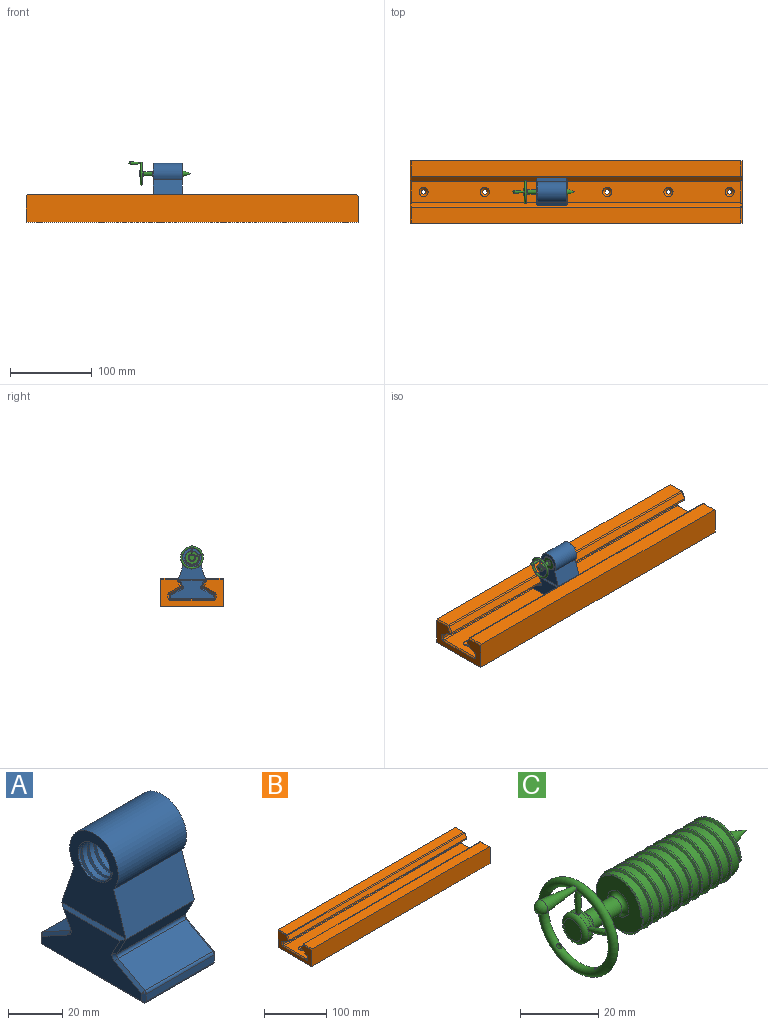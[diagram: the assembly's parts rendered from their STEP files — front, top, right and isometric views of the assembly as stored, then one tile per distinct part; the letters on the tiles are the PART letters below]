
ASSEMBLY  parts=3 mates=5
PART A: 54 faces, bbox 39.1x55.6x64.5 mm
  f0: plane 39.75x34.11mm, normal (1,0,0), area 733.2mm2, adj f44,f45,f46,f47,f48,f50,f51
  f1: plane 35.56x9.01mm, normal (0,0.88,-0.47), area 362.6mm2, adj f10,f26,f36,f44
  f2: plane 35.56x14.05mm, normal (0,0.48,0.88), area 569.9mm2, adj f10,f11,f22,f32
  f3: plane 35.56x3.32mm, normal (0,1,0), area 118mm2, adj f11,f12,f18,f31
  f4: plane 52.07x35.56mm, normal (0,0,-1), area 1851.6mm2, adj f12,f13,f17,f35
  f5: plane 35.56x3.32mm, normal (0,-1,0), area 118mm2, adj f13,f14,f21,f39
  f6: plane 35.56x14.05mm, normal (0,-0.48,0.88), area 569.9mm2, adj f14,f15,f25,f43
  f7: plane 35.56x9.01mm, normal (0,-0.88,-0.47), area 362.6mm2, adj f15,f29,f40,f46
  f8: plane 52.07x21.59mm, normal (1,0,0), area 724.5mm2, adj f31,f32,f34,f35,f36,f38,f39,f40
  f9: plane 52.07x21.59mm, normal (-1,0,0), area 724.5mm2, adj f17,f18,f21,f22,f24,f25,f26,f27
  f10: cylinder r=1.27mm len=35.56mm, axis (1,0,0), area 70.3mm2, adj f1,f2,f24,f34
  f11: cylinder r=1.27mm len=35.56mm, axis (-1,0,0), area 48.3mm2, adj f2,f3,f20,f30
  f12: cylinder r=1.27mm len=35.56mm, axis (1,0,0), area 70.9mm2, adj f3,f4,f16,f33
  f13: cylinder r=1.27mm len=35.56mm, axis (-1,0,0), area 70.9mm2, adj f4,f5,f19,f37
  f14: cylinder r=1.27mm len=35.56mm, axis (-1,0,0), area 48.3mm2, adj f5,f6,f23,f41
  f15: cylinder r=1.27mm len=35.56mm, axis (1,0,0), area 70.3mm2, adj f6,f7,f27,f42
  f16: cone r=1.27mm half-angle=45deg, axis (1,0,0), area 1.2mm2, adj f12,f17,f18
  f17: plane 52.07x1.27mm, normal (-0.71,0,-0.71), area 93.5mm2, adj f4,f9,f16,f19
  f18: plane 4.29x2.24mm, normal (-0.71,0.71,0), area 6mm2, adj f3,f9,f16,f20
  f19: cone r=1.27mm half-angle=45deg, axis (1,0,0), area 1.8mm2, adj f13,f17,f21
  f20: cone r=1.27mm half-angle=45deg, axis (1,0,0), area 1.8mm2, adj f11,f18,f22
  f21: plane 3.32x1.27mm, normal (-0.71,-0.71,0), area 6mm2, adj f5,f9,f19,f23
  f22: plane 14.66x8.83mm, normal (-0.71,0.34,0.62), area 28.8mm2, adj f2,f9,f20,f24
  f23: cone r=1.27mm half-angle=45deg, axis (1,0,0), area 1.2mm2, adj f14,f21,f25
  f24: cone r=2.54mm half-angle=45deg, axis (-1,0,0), area 5.3mm2, adj f9,f10,f22,f26
  f25: plane 14.66x8.83mm, normal (-0.71,-0.34,0.62), area 28.8mm2, adj f6,f9,f23,f27
  f26: plane 9.01x5.9mm, normal (-0.71,0.62,-0.33), area 16.4mm2, adj f1,f9,f24,f28
  f27: cone r=2.54mm half-angle=45deg, axis (-1,0,0), area 5.3mm2, adj f9,f15,f25,f29
  f28: plane 33.74x1.27mm, normal (-0.71,0,0.71), area 56.8mm2, adj f9,f26,f29,f49
  f29: plane 9.01x5.9mm, normal (-0.71,-0.62,-0.33), area 16.4mm2, adj f7,f9,f27,f28
  f30: cone r=1.27mm half-angle=45deg, axis (-1,0,0), area 0.8mm2, adj f11,f31,f32
  f31: plane 4.29x2.24mm, normal (0.71,0.71,0), area 6mm2, adj f3,f8,f30,f33
  f32: plane 14.98x9.14mm, normal (0.71,0.34,0.62), area 28.8mm2, adj f2,f8,f30,f34
  f33: cone r=1.27mm half-angle=45deg, axis (-1,0,0), area 2.4mm2, adj f12,f31,f35
  f34: cone r=2.54mm half-angle=45deg, axis (1,0,0), area 5.3mm2, adj f8,f10,f32,f36
  f35: plane 52.07x1.27mm, normal (0.71,0,-0.71), area 93.5mm2, adj f4,f8,f33,f37
  f36: plane 9.01x5.9mm, normal (0.71,0.62,-0.33), area 16.4mm2, adj f1,f8,f34,f38
  f37: cone r=1.27mm half-angle=45deg, axis (-1,0,0), area 1.8mm2, adj f13,f35,f39
  f38: plane 33.74x1.27mm, normal (0.71,0,0.71), area 56.8mm2, adj f8,f36,f40,f45
  f39: plane 3.32x1.27mm, normal (0.71,-0.71,0), area 6mm2, adj f5,f8,f37,f41
  f40: plane 9.01x5.9mm, normal (0.71,-0.62,-0.33), area 16.4mm2, adj f7,f8,f38,f42
  f41: cone r=1.27mm half-angle=45deg, axis (-1,0,0), area 1.2mm2, adj f14,f39,f43
  f42: cone r=2.54mm half-angle=45deg, axis (1,0,0), area 5.3mm2, adj f8,f15,f40,f43
  f43: plane 14.66x8.83mm, normal (0.71,-0.34,0.62), area 28.8mm2, adj f6,f8,f41,f42
  f44: plane 35.66x19.23mm, normal (0,0.95,0.32), area 724.6mm2, adj f0,f1,f45,f47,f49
  f45: plane 33.74x0.1mm, normal (0,0,-1), area 3.4mm2, adj f0,f38,f44,f46
  f46: plane 35.66x19.23mm, normal (0,-0.95,0.32), area 724.6mm2, adj f0,f7,f45,f47,f49
  f47: cylinder r=12.7mm len=35.66mm, axis (-1,0,0), area 1990.1mm2, adj f0,f44,f46,f49
  f48: cylinder r=8.26mm len=35.66mm, axis (-1,0,0), area 1233.4mm2, adj f0,f49,f50,f51,f52,f53
  f49: plane 39.87x34.23mm, normal (-1,0,0), area 732.3mm2, adj f28,f44,f46,f47,f48,f52,f53
  f50: plane 1.27x0.69mm, normal (0,0,1), area 0.4mm2, adj f0,f48,f53
  f51: bspline ~36.26x22mm, area 774.1mm2, adj f0,f48,f52,f53
  f52: plane 1.27x0.6mm, normal (0,0,-1), area 0.4mm2, adj f48,f49,f51
  f53: bspline ~36.35x22mm, area 798.9mm2, adj f48,f49,f50,f51
PART B: 68 faces, bbox 406.4x76.2x34.3 mm
  f0: plane 402.84x18.95mm, normal (0,0,1), area 7635.8mm2, adj f4,f21,f22,f67
  f1: plane 76.2x32.26mm, normal (1,0,0), area 1262.6mm2, adj f3,f4,f6,f51,f53,f55,f56,f57
  f2: plane 76.2x32.77mm, normal (-1,0,0), area 1345.9mm2, adj f3,f4,f6,f22,f23,f24,f25,f26
  f3: plane 406.4x34.29mm, normal (0,-1,0), area 13932.2mm2, adj f1,f2,f5,f6,f38,f51
  f4: plane 406.4x34.29mm, normal (0,1,0), area 13932.2mm2, adj f0,f1,f2,f6,f22,f67
  f5: plane 402.84x18.95mm, normal (0,0,1), area 7635.8mm2, adj f3,f14,f38,f51
  f6: plane 406.4x76.2mm, normal (0,0,-1), area 30809.2mm2, adj f1,f2,f3,f4,f39,f41,f43,f45
  f7: plane 402.84x7.64mm, normal (0,0.88,0.47), area 3486.2mm2, adj f14,f15,f36,f53
  f8: plane 402.84x12.78mm, normal (0,0.48,-0.88), area 5871.1mm2, adj f15,f16,f34,f55
  f9: plane 402.84x3.12mm, normal (0,1,0), area 1255.1mm2, adj f16,f17,f32,f57
  f10: plane 402.84x51.82mm, normal (0,0,1), area 20282.6mm2, adj f17,f18,f30,f40,f42,f44,f46,f48
  f11: plane 402.84x3.12mm, normal (0,-1,0), area 1255.1mm2, adj f18,f19,f28,f61
  f12: plane 402.84x12.78mm, normal (0,-0.48,-0.88), area 5871.1mm2, adj f19,f20,f26,f63
  f13: plane 402.84x7.64mm, normal (0,-0.88,0.47), area 3486.2mm2, adj f20,f21,f24,f65
  f14: cylinder r=2.03mm len=402.84mm, axis (-1,0,0), area 886.4mm2, adj f5,f7,f37,f52
  f15: cylinder r=2.03mm len=402.84mm, axis (1,0,0), area 1274.2mm2, adj f7,f8,f35,f54
  f16: cylinder r=2.03mm len=402.84mm, axis (-1,0,0), area 874.8mm2, adj f8,f9,f33,f56
  f17: cylinder r=2.03mm len=402.84mm, axis (-1,0,0), area 1285.8mm2, adj f9,f10,f31,f58
  f18: cylinder r=2.03mm len=402.84mm, axis (1,0,0), area 1285.8mm2, adj f10,f11,f29,f60
  f19: cylinder r=2.03mm len=402.84mm, axis (-1,0,0), area 874.8mm2, adj f11,f12,f27,f62
  f20: cylinder r=2.03mm len=402.84mm, axis (1,0,0), area 1274.2mm2, adj f12,f13,f25,f64
  f21: cylinder r=2.03mm len=402.84mm, axis (1,0,0), area 886.4mm2, adj f0,f13,f23,f66
  f22: plane 18.95x1.52mm, normal (-0.71,0,0.71), area 40.9mm2, adj f0,f2,f4,f23
  f23: cone r=0.51mm half-angle=45deg, axis (1,0,0), area 3mm2, adj f2,f21,f22,f24
  f24: plane 8.36x5.4mm, normal (-0.71,-0.62,0.33), area 18.7mm2, adj f2,f13,f23,f25
  f25: cone r=0.51mm half-angle=45deg, axis (1,0,0), area 4.3mm2, adj f2,f20,f24,f26
  f26: plane 13.51x8.35mm, normal (-0.71,-0.34,-0.62), area 31.4mm2, adj f2,f12,f25,f27
  f27: cone r=3.56mm half-angle=45deg, axis (-1,0,0), area 6.4mm2, adj f2,f19,f26,f28
  f28: plane 3.12x1.52mm, normal (-0.71,-0.71,0), area 6.7mm2, adj f2,f11,f27,f29
  f29: cone r=3.56mm half-angle=45deg, axis (-1,0,0), area 9.5mm2, adj f2,f18,f28,f30
  f30: plane 51.82x1.52mm, normal (-0.71,0,0.71), area 111.7mm2, adj f2,f10,f29,f31
  f31: cone r=3.56mm half-angle=45deg, axis (-1,0,0), area 9.5mm2, adj f2,f17,f30,f32
  f32: plane 3.12x1.52mm, normal (-0.71,0.71,0), area 6.7mm2, adj f2,f9,f31,f33
  f33: cone r=3.56mm half-angle=45deg, axis (-1,0,0), area 6.4mm2, adj f2,f16,f32,f34
  f34: plane 13.51x8.35mm, normal (-0.71,0.34,-0.62), area 31.4mm2, adj f2,f8,f33,f35
  f35: cone r=0.51mm half-angle=45deg, axis (1,0,0), area 4.3mm2, adj f2,f15,f34,f36
  f36: plane 8.36x5.4mm, normal (-0.71,0.62,0.33), area 18.7mm2, adj f2,f7,f35,f37
  f37: cone r=0.51mm half-angle=45deg, axis (1,0,0), area 3mm2, adj f2,f14,f36,f38
  f38: plane 18.95x1.52mm, normal (-0.71,0,0.71), area 40.9mm2, adj f2,f3,f5,f37
  f39: cylinder r=2.9mm len=6.19mm, axis (0,0,1), area 112.8mm2, adj f6,f40
  f40: cone r=2.9mm half-angle=45deg, axis (0,0,1), area 102mm2, adj f10,f39
  f41: cylinder r=2.9mm len=6.19mm, axis (0,0,1), area 112.8mm2, adj f6,f42
  f42: cone r=2.9mm half-angle=45deg, axis (0,0,1), area 102mm2, adj f10,f41
  f43: cylinder r=2.9mm len=6.19mm, axis (0,0,1), area 112.8mm2, adj f6,f44
  f44: cone r=2.9mm half-angle=45deg, axis (0,0,1), area 102mm2, adj f10,f43
  f45: cylinder r=2.9mm len=6.19mm, axis (0,0,1), area 112.8mm2, adj f6,f46
  f46: cone r=2.9mm half-angle=45deg, axis (0,0,1), area 102mm2, adj f10,f45
  f47: cylinder r=2.9mm len=6.19mm, axis (0,0,1), area 112.8mm2, adj f6,f48
  f48: cone r=2.9mm half-angle=45deg, axis (0,0,1), area 102mm2, adj f10,f47
  f49: cylinder r=2.9mm len=6.19mm, axis (0,0,1), area 112.8mm2, adj f6,f50
  f50: cone r=2.9mm half-angle=45deg, axis (0,0,1), area 102mm2, adj f10,f49
  f51: plane 18.95x2.03mm, normal (0.71,0,0.71), area 54.5mm2, adj f1,f3,f5,f52
  f52: cone r=2.03mm half-angle=45deg, axis (-1,0,0), area 3.2mm2, adj f14,f51,f53
  f53: plane 8.6x5.85mm, normal (0.71,0.62,0.33), area 24.9mm2, adj f1,f7,f52,f54
  f54: cone r=2.03mm half-angle=45deg, axis (-1,0,0), area 4.5mm2, adj f15,f53,f55
  f55: plane 13.75x8.8mm, normal (0.71,0.34,-0.62), area 41.9mm2, adj f1,f8,f54,f56
  f56: cone r=4.06mm half-angle=45deg, axis (1,0,0), area 9.4mm2, adj f1,f16,f55,f57
  f57: plane 3.12x2.03mm, normal (0.71,0.71,0), area 9mm2, adj f1,f9,f56,f58
  f58: cone r=4.06mm half-angle=45deg, axis (1,0,0), area 13.8mm2, adj f1,f17,f57,f59
  f59: plane 51.82x2.03mm, normal (0.71,0,0.71), area 148.9mm2, adj f1,f10,f58,f60
  f60: cone r=4.06mm half-angle=45deg, axis (1,0,0), area 13.8mm2, adj f1,f18,f59,f61
  f61: plane 3.12x2.03mm, normal (0.71,-0.71,0), area 9mm2, adj f1,f11,f60,f62
  f62: cone r=4.06mm half-angle=45deg, axis (1,0,0), area 9.4mm2, adj f1,f19,f61,f63
  f63: plane 13.75x8.8mm, normal (0.71,-0.34,-0.62), area 41.9mm2, adj f1,f12,f62,f64
  f64: cone r=2.03mm half-angle=45deg, axis (-1,0,0), area 4.5mm2, adj f20,f63,f65
  f65: plane 8.6x5.85mm, normal (0.71,-0.62,0.33), area 24.9mm2, adj f1,f13,f64,f66
  f66: cone r=2.03mm half-angle=45deg, axis (-1,0,0), area 3.2mm2, adj f21,f65,f67
  f67: plane 18.95x2.03mm, normal (0.71,0,0.71), area 54.5mm2, adj f0,f1,f4,f66
PART C: 28 faces, bbox 76.1x30.6x30.6 mm
  f0: torus R=12.71mm, axis (-1,0,0), area 627.1mm2, adj f1,f2,f4,f5,f24,f25,f26,f27
  f1: sphere r=0.64mm, area 5.1mm2, adj f0,f2
  f2: cone r=0.63mm half-angle=6.4deg, axis (-1,0,0), area 95.6mm2, adj f0,f1,f3,f4
  f3: sphere r=1.97mm, area 27.1mm2, adj f2
  f4: sphere r=0.64mm, area 5.1mm2, adj f0,f2
  f5: revolved ~7.18x3.49mm, area 69.1mm2, adj f0,f6
  f6: cylinder r=4.45mm len=8.89mm, axis (1,0,0), area 30.8mm2, adj f5,f7,f22,f24,f25,f26,f27
  f7: bspline ~8.9x8.9mm, area 44.8mm2, adj f6,f8
  f8: bspline ~7.62x7.62mm, area 29.7mm2, adj f7,f9
  f9: cylinder r=2.54mm len=10.16mm, axis (1,0,0), area 162.1mm2, adj f8,f10
  f10: torus R=3.81mm, axis (-1,0,0), area 37.6mm2, adj f9,f11
  f11: plane 17.13x16.31mm, normal (-1,0,0), area 161mm2, adj f10,f12,f19,f20,f21
  f12: plane 0.82x0.55mm, normal (0,0,1), area 0.3mm2, adj f11,f13,f18,f19,f21
  f13: cylinder r=8.26mm len=35.15mm, axis (-1,0,0), area 1378.1mm2, adj f12,f14,f17,f18,f20,f21
  f14: plane 0.82x0.55mm, normal (0,0,-1), area 0.3mm2, adj f13,f15,f17,f19,f20
  f15: plane 17.14x16.31mm, normal (1,0,0), area 161mm2, adj f14,f16,f17,f18,f19
  f16: cone r=3.81mm half-angle=20deg, axis (-1,0,0), area 133.3mm2, adj f15
  f17: cone r=8.26mm half-angle=45deg, axis (-1,0,0), area 14.5mm2, adj f13,f14,f15,f18
  f18: bspline ~36.35x21.41mm, area 343.6mm2, adj f12,f13,f15,f17,f19
  f19: bspline ~36.23x17.92mm, area 267.4mm2, adj f11,f12,f14,f15,f18,f20
  f20: bspline ~36.35x21.41mm, area 343.6mm2, adj f11,f13,f14,f19,f21
  f21: cone r=8mm half-angle=45deg, axis (1,0,0), area 14.5mm2, adj f11,f12,f13,f20
  f22: torus R=3.17mm, axis (-1,0,0), area 49.9mm2, adj f6,f23
  f23: plane 6.35x6.35mm, normal (-1,0,0), area 31.7mm2, adj f22
  f24: revolved ~6.65x5.35mm, area 0.4mm2, adj f0,f6
  f25: revolved ~6.65x5.35mm, area 0mm2, adj f0,f6
  f26: revolved ~7.32x3.52mm, area 0.5mm2, adj f0,f6
  f27: revolved ~7.26x1.65mm, area 34.7mm2, adj f0,f6
PLACE A t=(-251.9,0,-0.64)mm
PLACE B t=(-406.4,0,0)mm
PLACE C rot(axis=(0,0,-1),0deg) t=(-251.9,0,-0.63)mm
MATE parallel C.f0 <-> A.f47  axis (1,0,0) through (-214.97,38.1,59.69)mm
MATE pin_slot A.f4 <-> B.f10  axis (0,0,-1) through (-250.63,38.1,8.89)mm
MATE revolute C.f0 <-> A.f47  axis (1,0,0) through (-214.97,38.1,59.69)mm
MATE slider C.f0 <-> A.f47  axis (1,0,0) through (-214.97,38.1,59.69)mm
MATE parallel A.f9 <-> B.f2  axis (-1,0,0) through (-251.9,38.1,19.19)mm
